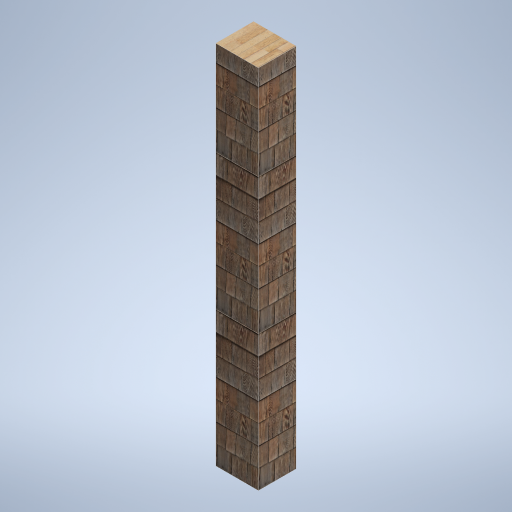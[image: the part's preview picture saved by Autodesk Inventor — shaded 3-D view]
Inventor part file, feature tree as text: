
AUTODESK INVENTOR PART (.ipt)
format: ipt  version: 2024.2 (Build 282272000, 272)  size: 346,112 bytes
history: native  units: mm
features: extrude x1, sketch x1
ambient origin geometry x8: Origin, YZ Plane, XZ Plane, XY Plane, X Axis, Y Axis, Z Axis, Center Point
bodies: Solid1 (feature_tree)
feature tree (2):
  extrude  "Extrusion1"  Depth=310.0mm
  sketch  "Sketch1"  dims[d0=350.0mm d1=310.0mm d2=3000.0mm d3=0.0mm]
